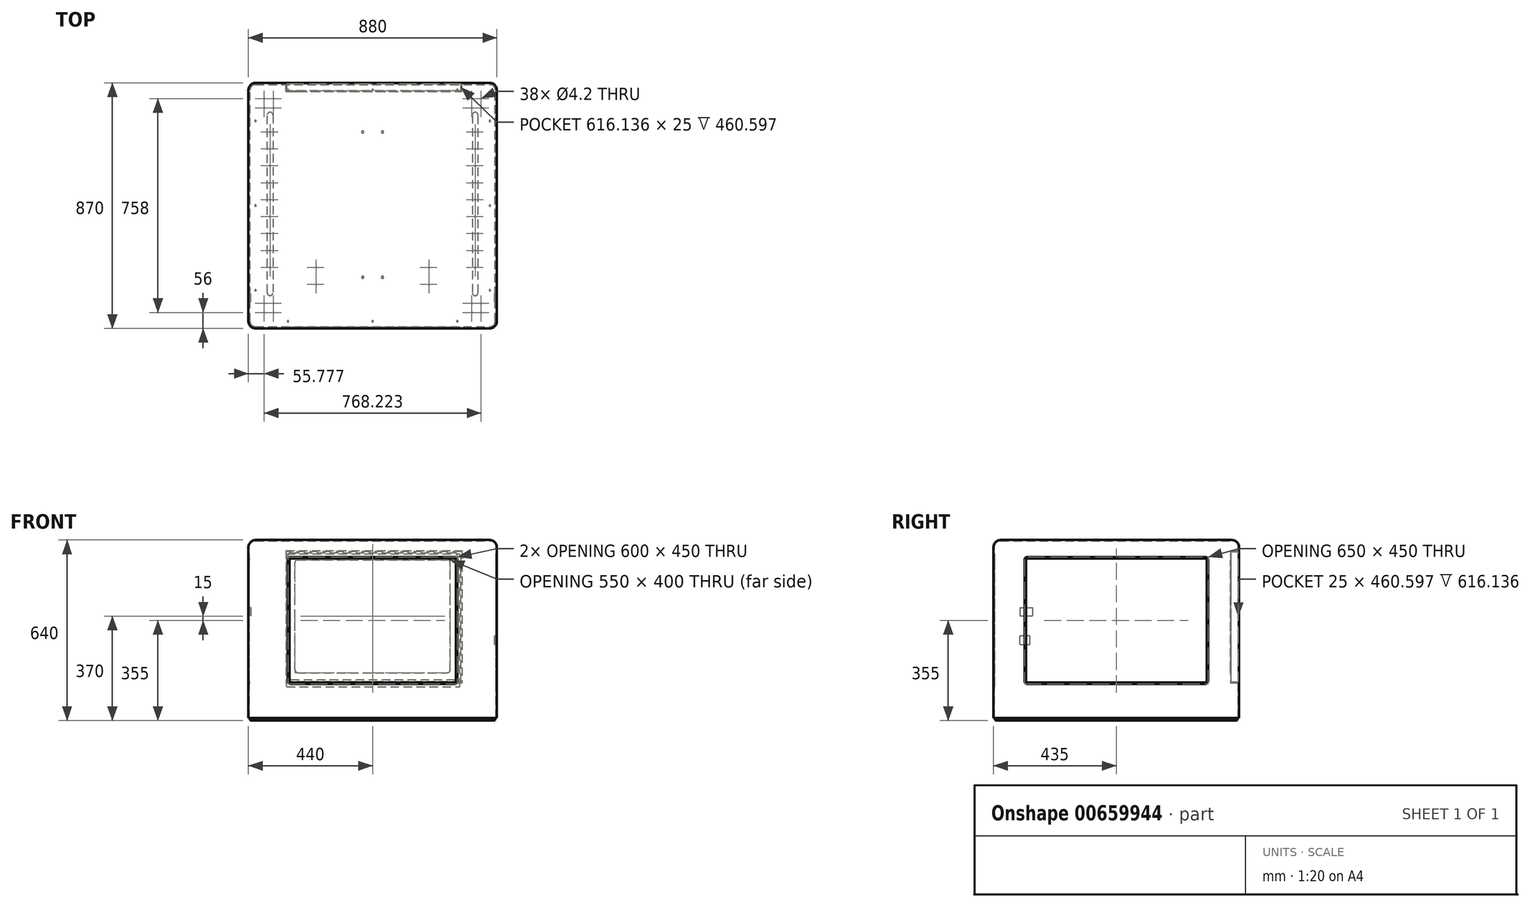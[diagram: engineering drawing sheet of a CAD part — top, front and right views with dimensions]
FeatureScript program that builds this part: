
annotation { "Feature Type Name" : "Feature", "Feature Type Description" : "" }
export const myFeature = defineFeature(function(context is Context, id is Id, definition is map)
    precondition{}
    {
        {
            var Q0;
            Q0=qCreatedBy(makeId("Top.planeOp"),FACE);
            var sketch = newSketch(context, id + "F0", { "sketchPlane" : qUnion([Q0])});
            skLineSegment(sketch, "E0.bottom", {"start": v(-440, -435) * mm, "end": v(440, -435) * mm});
            skLineSegment(sketch, "E0.top", {"start": v(-440, 435) * mm, "end": v(440, 435) * mm});
            skLineSegment(sketch, "E0.left", {"start": v(-440, -435) * mm, "end": v(-440, 435) * mm});
            skLineSegment(sketch, "E0.right", {"start": v(440, -435) * mm, "end": v(440, 435) * mm});
            skPoint(sketch, "E0.middle", {"position": v(0, 0) * mm});
            skSolve(sketch);
        }
        {
            var Q0;
            Q0 = qSketchRegion(id + "F0", true);
            extrude(context, id + "F1", {"entities" : qUnion([Q0]), "depth" : 630 * mm, "offsetDistance" : 25 * mm});
        }
        {
            var Q0;
            Q0=makeQuery(id+"F1.opExtrude","CAP_EDGE",EDGE,{"disambiguationData":[OSD([sQuery(id+"F0.wireOp",EDGE,"E0.right")])],"isStart":false});
            var Q1;
            Q1=makeQuery(id+"F1.opExtrude","CAP_EDGE",EDGE,{"disambiguationData":[OSD([sQuery(id+"F0.wireOp",EDGE,"E0.left")])],"isStart":false});
            fillet(context, id + "F2", {"entities" : qUnion([Q0, Q1]), "radius" : 25 * mm, "tangentPropagation" : true, "allowEdgeOverflow" : false});
        }
        {
            var Q0;
            Q0=makeQuery(id+"F1.opExtrude","CAP_EDGE",EDGE,{"disambiguationData":[OSD([sQuery(id+"F0.wireOp",EDGE,"E0.bottom")])],"isStart":false});
            var Q1;
            Q1=makeQuery(id+"F1.opExtrude","CAP_EDGE",EDGE,{"disambiguationData":[OSD([sQuery(id+"F0.wireOp",EDGE,"E0.top")])],"isStart":false});
            fillet(context, id + "F3", {"entities" : qUnion([Q0, Q1]), "radius" : 25 * mm, "tangentPropagation" : true, "allowEdgeOverflow" : false});
        }
        {
            var Q0;
            Q0=makeQuery(id+"F1.opExtrude","CAP_FACE",FACE,{"disambiguationData":[OSD([sQuery(id+"F0.wireOp",EDGE,"E0.bottom"),sQuery(id+"F0.wireOp",EDGE,"E0.top"),sQuery(id+"F0.wireOp",EDGE,"E0.left"),sQuery(id+"F0.wireOp",EDGE,"E0.right")])],"isStart":true});
            shell(context, id + "F4", {"entities" : qUnion([Q0]), "thickness" : 3 * mm});
        }
        {
            var Q0;
            Q0=makeQuery(id+"F1.opExtrude","SWEPT_FACE",FACE,{"disambiguationData":[OSD([sQuery(id+"F0.wireOp",EDGE,"E0.top")])]});
            var sketch = newSketch(context, id + "F5", { "sketchPlane" : qUnion([Q0])});
            skLineSegment(sketch, "E1.bottom", {"start": v(290, 135) * mm, "end": v(-290, 135) * mm});
            skLineSegment(sketch, "E1.top", {"start": v(290, 585) * mm, "end": v(-290, 585) * mm});
            skLineSegment(sketch, "E1.left", {"start": v(300, 145) * mm, "end": v(300, 575) * mm});
            skLineSegment(sketch, "E1.right", {"start": v(-300, 145) * mm, "end": v(-300, 575) * mm});
            skPoint(sketch, "E1.middle", {"position": v(0, 360) * mm});
            skPoint(sketch, "E2.visualSharp", {"position": v(-300, 585) * mm});
            skArc(sketch, "E2.filletArc", {"start": v(-290, 585) * mm, "mid": v(-297.07, 582.07) * mm, "end": v(-300, 575) * mm});
            skPoint(sketch, "E3.visualSharp", {"position": v(300, 585) * mm});
            skArc(sketch, "E3.filletArc", {"start": v(300, 575) * mm, "mid": v(297.07, 582.07) * mm, "end": v(290, 585) * mm});
            skPoint(sketch, "E4.visualSharp", {"position": v(300, 135) * mm});
            skArc(sketch, "E4.filletArc", {"start": v(290, 135) * mm, "mid": v(297.07, 137.93) * mm, "end": v(300, 145) * mm});
            skPoint(sketch, "E5.visualSharp", {"position": v(-300, 135) * mm});
            skArc(sketch, "E5.filletArc", {"start": v(-300, 145) * mm, "mid": v(-297.07, 137.93) * mm, "end": v(-290, 135) * mm});
            skSolve(sketch);
        }
        {
            var Q0;
            Q0 = qSketchRegion(id + "F5", true);
            extrude(context, id + "F6", {"entities" : qUnion([Q0]), "operationType" : NewBodyOperationType.REMOVE, "oppositeDirection" : true, "depth" : 25 * mm, "offsetDistance" : 25 * mm});
        }
        {
            var Q0;
            Q0=makeQuery(id+"F1.opExtrude","SWEPT_FACE",FACE,{"disambiguationData":[OSD([sQuery(id+"F0.wireOp",EDGE,"E0.bottom")])]});
            var sketch = newSketch(context, id + "F7", { "sketchPlane" : qUnion([Q0])});
            skLineSegment(sketch, "E6.bottom", {"start": v(290, 120) * mm, "end": v(-290, 120) * mm});
            skLineSegment(sketch, "E6.top", {"start": v(290, 570) * mm, "end": v(-290, 570) * mm});
            skLineSegment(sketch, "E6.left", {"start": v(300, 130) * mm, "end": v(300, 560) * mm});
            skLineSegment(sketch, "E6.right", {"start": v(-300, 130) * mm, "end": v(-300, 560) * mm});
            skPoint(sketch, "E6.middle", {"position": v(0, 345) * mm});
            skPoint(sketch, "E7.visualSharp", {"position": v(300, 570) * mm});
            skArc(sketch, "E7.filletArc", {"start": v(300, 560) * mm, "mid": v(297.07, 567.07) * mm, "end": v(290, 570) * mm});
            skPoint(sketch, "E8.visualSharp", {"position": v(-300, 570) * mm});
            skArc(sketch, "E8.filletArc", {"start": v(-290, 570) * mm, "mid": v(-297.07, 567.07) * mm, "end": v(-300, 560) * mm});
            skPoint(sketch, "E9.visualSharp", {"position": v(300, 120) * mm});
            skArc(sketch, "E9.filletArc", {"start": v(290, 120) * mm, "mid": v(297.07, 122.93) * mm, "end": v(300, 130) * mm});
            skPoint(sketch, "E10.visualSharp", {"position": v(-300, 120) * mm});
            skArc(sketch, "E10.filletArc", {"start": v(-300, 130) * mm, "mid": v(-297.07, 122.93) * mm, "end": v(-290, 120) * mm});
            skArc(sketch, "E11.0", {"start": v(295, 560) * mm, "mid": v(293.54, 563.54) * mm, "end": v(290, 565) * mm});
            skLineSegment(sketch, "E11.1", {"start": v(295, 130) * mm, "end": v(295, 560) * mm});
            skLineSegment(sketch, "E11.2", {"start": v(290, 565) * mm, "end": v(-290, 565) * mm});
            skArc(sketch, "E11.3", {"start": v(290, 125) * mm, "mid": v(293.54, 126.46) * mm, "end": v(295, 130) * mm});
            skArc(sketch, "E11.4", {"start": v(-290, 565) * mm, "mid": v(-293.54, 563.54) * mm, "end": v(-295, 560) * mm});
            skLineSegment(sketch, "E11.5", {"start": v(-295, 130) * mm, "end": v(-295, 560) * mm});
            skArc(sketch, "E11.6", {"start": v(-295, 130) * mm, "mid": v(-293.54, 126.46) * mm, "end": v(-290, 125) * mm});
            skLineSegment(sketch, "E11.7", {"start": v(290, 125) * mm, "end": v(-290, 125) * mm});
            skSolve(sketch);
        }
        {
            var Q0;
            Q0 = qSketchRegion(id + "F7", true);
            extrude(context, id + "F8", {"entities" : qUnion([Q0]), "operationType" : NewBodyOperationType.REMOVE, "oppositeDirection" : true, "depth" : 25 * mm, "offsetDistance" : 25 * mm});
        }
        {
            var Q0;
            {var subQ2=sQuery(id+"F0.wireOp",EDGE,"E0.bottom");var subQ3=makeQuery(id+"F1.opExtrude","SWEPT_FACE",FACE,{"disambiguationData":[OSD([subQ2])]});Q0=makeQuery(id+"F8.boolean.opBoolean","SPLIT",FACE,{"disambiguationData":[TD([makeQuery(id+"F8.opExtrude","SWEPT_FACE",FACE,{"disambiguationData":[OSD([sQuery(id+"F7.wireOp",EDGE,"E6.bottom")])]})])],"derivedFrom":makeQuery(id+"F4.opShell","OFFSET_FACE",FACE,{"disambiguationData":[OSD([subQ2]),TDD([subQ3])]})});}
            var sketch = newSketch(context, id + "F9", { "sketchPlane" : qUnion([Q0])});
            skLineSegment(sketch, "E12.bottom", {"start": v(304.63, 110.16) * mm, "end": v(-308.53, 110.16) * mm});
            skLineSegment(sketch, "E12.top", {"start": v(304.63, 580.55) * mm, "end": v(-308.53, 580.55) * mm});
            skLineSegment(sketch, "E12.left", {"start": v(304.63, 110.16) * mm, "end": v(304.63, 580.55) * mm});
            skLineSegment(sketch, "E12.right", {"start": v(-308.53, 110.16) * mm, "end": v(-308.53, 580.55) * mm});
            skSolve(sketch);
        }
        {
            var Q0;
            Q0 = qSketchRegion(id + "F9", true);
            extrude(context, id + "F10", {"entities" : qUnion([Q0]), "depth" : 2 * mm, "offsetDistance" : 25 * mm});
        }
        {
            var Q0;
            Q0=makeQuery(id+"F1.opExtrude","SWEPT_FACE",FACE,{"disambiguationData":[OSD([sQuery(id+"F0.wireOp",EDGE,"E0.right")])]});
            var sketch = newSketch(context, id + "F11", { "sketchPlane" : qUnion([Q0])});
            skLineSegment(sketch, "E13.bottom", {"start": v(315, 570) * mm, "end": v(-315, 570) * mm});
            skLineSegment(sketch, "E13.top", {"start": v(315, 120) * mm, "end": v(-315, 120) * mm});
            skLineSegment(sketch, "E13.left", {"start": v(325, 560) * mm, "end": v(325, 130) * mm});
            skLineSegment(sketch, "E13.right", {"start": v(-325, 560) * mm, "end": v(-325, 130) * mm});
            skPoint(sketch, "E13.middle", {"position": v(0, 345) * mm});
            skPoint(sketch, "E13.middle.positionSnap0", {"position": v(0, 0) * mm});
            skPoint(sketch, "E13.centerSnap0", {"position": v(0, 0) * mm});
            skPoint(sketch, "E14.visualSharp", {"position": v(325, 570) * mm});
            skArc(sketch, "E14.filletArc", {"start": v(325, 560) * mm, "mid": v(322.07, 567.07) * mm, "end": v(315, 570) * mm});
            skPoint(sketch, "E15.visualSharp", {"position": v(325, 120) * mm});
            skArc(sketch, "E15.filletArc", {"start": v(315, 120) * mm, "mid": v(322.07, 122.93) * mm, "end": v(325, 130) * mm});
            skPoint(sketch, "E16.visualSharp", {"position": v(-325, 120) * mm});
            skArc(sketch, "E16.filletArc", {"start": v(-325, 130) * mm, "mid": v(-322.07, 122.93) * mm, "end": v(-315, 120) * mm});
            skPoint(sketch, "E17.visualSharp", {"position": v(-325, 570) * mm});
            skArc(sketch, "E17.filletArc", {"start": v(-315, 570) * mm, "mid": v(-322.07, 567.07) * mm, "end": v(-325, 560) * mm});
            skArc(sketch, "E18.0", {"start": v(320, 560) * mm, "mid": v(318.54, 563.54) * mm, "end": v(315, 565) * mm});
            skLineSegment(sketch, "E18.1", {"start": v(320, 560) * mm, "end": v(320, 130) * mm});
            skLineSegment(sketch, "E18.2", {"start": v(315, 565) * mm, "end": v(-315, 565) * mm});
            skArc(sketch, "E18.3", {"start": v(315, 125) * mm, "mid": v(318.54, 126.46) * mm, "end": v(320, 130) * mm});
            skArc(sketch, "E18.4", {"start": v(-315, 565) * mm, "mid": v(-318.54, 563.54) * mm, "end": v(-320, 560) * mm});
            skLineSegment(sketch, "E18.5", {"start": v(-320, 560) * mm, "end": v(-320, 130) * mm});
            skArc(sketch, "E18.6", {"start": v(-320, 130) * mm, "mid": v(-318.54, 126.46) * mm, "end": v(-315, 125) * mm});
            skLineSegment(sketch, "E18.7", {"start": v(315, 125) * mm, "end": v(-315, 125) * mm});
            skSolve(sketch);
        }
        {
            var Q0;
            Q0 = qSketchRegion(id + "F11", true);
            extrude(context, id + "F12", {"entities" : qUnion([Q0]), "operationType" : NewBodyOperationType.REMOVE, "oppositeDirection" : true, "depth" : 2500 * mm, "offsetDistance" : 25 * mm});
        }
        {
            var Q0;
            {var subQ0=sQuery(id+"F0.wireOp",EDGE,"E0.left");Q0=makeQuery(id+"F12.boolean.opBoolean","SPLIT",FACE,{"disambiguationData":[TD([makeQuery(id+"F12.opExtrude","SWEPT_FACE",FACE,{"disambiguationData":[OSD([sQuery(id+"F11.wireOp",EDGE,"E13.bottom")])]})])],"derivedFrom":makeQuery(id+"F4.opShell","OFFSET_FACE",FACE,{"disambiguationData":[OSD([subQ0]),TDD([makeQuery(id+"F1.opExtrude","SWEPT_FACE",FACE,{"disambiguationData":[OSD([subQ0])]})])]})});}
            var sketch = newSketch(context, id + "F13", { "sketchPlane" : qUnion([Q0])});
            skLineSegment(sketch, "E19.bottom", {"start": v(-341.34, 390.67) * mm, "end": v(-296.45, 390.67) * mm});
            skLineSegment(sketch, "E19.top", {"start": v(-341.34, 361.64) * mm, "end": v(-296.45, 361.64) * mm});
            skLineSegment(sketch, "E19.left", {"start": v(-341.34, 390.67) * mm, "end": v(-341.34, 361.64) * mm});
            skLineSegment(sketch, "E19.right", {"start": v(-296.45, 390.67) * mm, "end": v(-296.45, 361.64) * mm});
            skSolve(sketch);
        }
        {
            var Q0;
            Q0 = qSketchRegion(id + "F13", true);
            extrude(context, id + "F14", {"entities" : qUnion([Q0]), "operationType" : NewBodyOperationType.ADD, "depth" : 5 * mm, "offsetDistance" : 25 * mm});
        }
        {
            var Q0;
            {var subQ1=sQuery(id+"F0.wireOp",EDGE,"E0.right");Q0=makeQuery(id+"F12.boolean.opBoolean","SPLIT",FACE,{"disambiguationData":[TD([makeQuery(id+"F12.opExtrude","SWEPT_FACE",FACE,{"disambiguationData":[OSD([sQuery(id+"F11.wireOp",EDGE,"E13.bottom")])]})])],"derivedFrom":makeQuery(id+"F4.opShell","OFFSET_FACE",FACE,{"disambiguationData":[OSD([subQ1]),TDD([makeQuery(id+"F1.opExtrude","SWEPT_FACE",FACE,{"disambiguationData":[OSD([subQ1])]})])]})});}
            var sketch = newSketch(context, id + "F15", { "sketchPlane" : qUnion([Q0])});
            skLineSegment(sketch, "E20.bottom", {"start": v(340.75, 259.87) * mm, "end": v(305.28, 259.87) * mm});
            skLineSegment(sketch, "E20.top", {"start": v(340.75, 291.6) * mm, "end": v(305.28, 291.6) * mm});
            skLineSegment(sketch, "E20.left", {"start": v(340.75, 259.87) * mm, "end": v(340.75, 291.6) * mm});
            skLineSegment(sketch, "E20.right", {"start": v(305.28, 259.87) * mm, "end": v(305.28, 291.6) * mm});
            skSolve(sketch);
        }
        {
            var Q0;
            Q0 = qSketchRegion(id + "F15", true);
            extrude(context, id + "F16", {"entities" : qUnion([Q0]), "operationType" : NewBodyOperationType.ADD, "depth" : 5 * mm, "offsetDistance" : 25 * mm});
        }
        {
            var Q0;
            Q0=makeQuery(id+"F1.opExtrude","CAP_FACE",FACE,{"disambiguationData":[OSD([sQuery(id+"F0.wireOp",EDGE,"E0.bottom"),sQuery(id+"F0.wireOp",EDGE,"E0.top"),sQuery(id+"F0.wireOp",EDGE,"E0.left"),sQuery(id+"F0.wireOp",EDGE,"E0.right")])],"isStart":true});
            var sketch = newSketch(context, id + "F17", { "sketchPlane" : qUnion([Q0])});
            skLineSegment(sketch, "E21.0", {"start": v(437, 410) * mm, "end": v(437, -410) * mm});
            skArc(sketch, "E22.0", {"start": v(415, -432) * mm, "mid": v(430.56, -425.56) * mm, "end": v(437, -410) * mm});
            skLineSegment(sketch, "E23.0", {"start": v(-415, -432) * mm, "end": v(415, -432) * mm});
            skArc(sketch, "E24.0", {"start": v(-437, -410) * mm, "mid": v(-430.56, -425.56) * mm, "end": v(-415, -432) * mm});
            skLineSegment(sketch, "E25.0", {"start": v(-437, 410) * mm, "end": v(-437, -410) * mm});
            skArc(sketch, "E26.0", {"start": v(-415, 432) * mm, "mid": v(-430.56, 425.56) * mm, "end": v(-437, 410) * mm});
            skLineSegment(sketch, "E27.0", {"start": v(-415, 432) * mm, "end": v(415, 432) * mm});
            skArc(sketch, "E28.0", {"start": v(437, 410) * mm, "mid": v(430.56, 425.56) * mm, "end": v(415, 432) * mm});
            skArc(sketch, "E29.0", {"start": v(434, 410) * mm, "mid": v(428.44, 423.44) * mm, "end": v(415, 429) * mm});
            skLineSegment(sketch, "E29.1", {"start": v(-415, 429) * mm, "end": v(415, 429) * mm});
            skLineSegment(sketch, "E29.2", {"start": v(434, 410) * mm, "end": v(434, -410) * mm});
            skArc(sketch, "E29.3", {"start": v(-415, 429) * mm, "mid": v(-428.44, 423.44) * mm, "end": v(-434, 410) * mm});
            skArc(sketch, "E29.4", {"start": v(415, -429) * mm, "mid": v(428.44, -423.44) * mm, "end": v(434, -410) * mm});
            skLineSegment(sketch, "E29.5", {"start": v(-415, -429) * mm, "end": v(415, -429) * mm});
            skArc(sketch, "E29.6", {"start": v(-434, -410) * mm, "mid": v(-428.44, -423.44) * mm, "end": v(-415, -429) * mm});
            skLineSegment(sketch, "E29.7", {"start": v(-434, 410) * mm, "end": v(-434, -410) * mm});
            skLineSegment(sketch, "E30.bottom", {"start": v(-384, 379) * mm, "end": v(-351, 379) * mm, "construction": true});
            skLineSegment(sketch, "E30.top", {"start": v(-384, 346) * mm, "end": v(-351, 346) * mm, "construction": true});
            skLineSegment(sketch, "E30.left", {"start": v(-384, 379) * mm, "end": v(-384, 346) * mm, "construction": true});
            skLineSegment(sketch, "E30.right", {"start": v(-351, 379) * mm, "end": v(-351, 346) * mm, "construction": true});
            skCircle(sketch, "E31", {"center": v(-384, 379) * mm, "radius": 2.5 * mm});
            skCircle(sketch, "E32", {"center": v(-351, 379) * mm, "radius": 2.5 * mm});
            skCircle(sketch, "E33", {"center": v(-351, 346) * mm, "radius": 2.5 * mm});
            skCircle(sketch, "E34", {"center": v(-384, 346) * mm, "radius": 2.5 * mm});
            skCircle(sketch, "E35", {"center": v(351, 379) * mm, "radius": 2.5 * mm});
            skCircle(sketch, "E36", {"center": v(384, 379) * mm, "radius": 2.5 * mm});
            skCircle(sketch, "E37", {"center": v(384, 346) * mm, "radius": 2.5 * mm});
            skCircle(sketch, "E38", {"center": v(351, 346) * mm, "radius": 2.5 * mm});
            skCircle(sketch, "E39", {"center": v(-384, -346) * mm, "radius": 2.5 * mm});
            skCircle(sketch, "E40", {"center": v(-351, -379) * mm, "radius": 2.5 * mm});
            skCircle(sketch, "E41", {"center": v(-351, -346) * mm, "radius": 2.5 * mm});
            skCircle(sketch, "E42", {"center": v(-384.22, -379) * mm, "radius": 2.5 * mm});
            skCircle(sketch, "E43", {"center": v(351, -346) * mm, "radius": 2.5 * mm});
            skCircle(sketch, "E44", {"center": v(384, -346) * mm, "radius": 2.5 * mm});
            skCircle(sketch, "E45", {"center": v(384, -379) * mm, "radius": 2.5 * mm});
            skCircle(sketch, "E46", {"center": v(351, -379) * mm, "radius": 2.5 * mm});
            skSolve(sketch);
        }
        {
            var Q0;
            Q0=makeQuery(id+"F17.imprint","IMPRINT",FACE,{"disambiguationData":[TD([[makeQuery(id+"F17.imprint","IMPRINT",EDGE,{"derivedFrom":sQuery(id+"F17.wireOp",EDGE,"E29.0")}),1.0]])]});
            var Q1;
            Q1=makeQuery(id+"F17.imprint","IMPRINT",FACE,{"disambiguationData":[TD([[makeQuery(id+"F17.imprint","IMPRINT",EDGE,{"derivedFrom":sQuery(id+"F17.wireOp",EDGE,"E31")}),1.0]])]});
            var Q2;
            Q2=makeQuery(id+"F17.imprint","IMPRINT",FACE,{"disambiguationData":[TD([[makeQuery(id+"F17.imprint","IMPRINT",EDGE,{"derivedFrom":sQuery(id+"F17.wireOp",EDGE,"E32")}),1.0]])]});
            var Q3;
            Q3=makeQuery(id+"F17.imprint","IMPRINT",FACE,{"disambiguationData":[TD([[makeQuery(id+"F17.imprint","IMPRINT",EDGE,{"derivedFrom":sQuery(id+"F17.wireOp",EDGE,"E33")}),1.0]])]});
            var Q4;
            Q4=makeQuery(id+"F17.imprint","IMPRINT",FACE,{"disambiguationData":[TD([[makeQuery(id+"F17.imprint","IMPRINT",EDGE,{"derivedFrom":sQuery(id+"F17.wireOp",EDGE,"E34")}),1.0]])]});
            var Q5;
            Q5=makeQuery(id+"F17.imprint","IMPRINT",FACE,{"disambiguationData":[TD([[makeQuery(id+"F17.imprint","IMPRINT",EDGE,{"derivedFrom":sQuery(id+"F17.wireOp",EDGE,"E39")}),1.0]])]});
            var Q6;
            Q6=makeQuery(id+"F17.imprint","IMPRINT",FACE,{"disambiguationData":[TD([[makeQuery(id+"F17.imprint","IMPRINT",EDGE,{"derivedFrom":sQuery(id+"F17.wireOp",EDGE,"E41")}),1.0]])]});
            var Q7;
            Q7=makeQuery(id+"F17.imprint","IMPRINT",FACE,{"disambiguationData":[TD([[makeQuery(id+"F17.imprint","IMPRINT",EDGE,{"derivedFrom":sQuery(id+"F17.wireOp",EDGE,"E40")}),1.0]])]});
            var Q8;
            Q8=makeQuery(id+"F17.imprint","IMPRINT",FACE,{"disambiguationData":[TD([[makeQuery(id+"F17.imprint","IMPRINT",EDGE,{"derivedFrom":sQuery(id+"F17.wireOp",EDGE,"E42")}),1.0]])]});
            var Q9;
            Q9=makeQuery(id+"F17.imprint","IMPRINT",FACE,{"disambiguationData":[TD([[makeQuery(id+"F17.imprint","IMPRINT",EDGE,{"derivedFrom":sQuery(id+"F17.wireOp",EDGE,"E45")}),1.0]])]});
            var Q10;
            Q10=makeQuery(id+"F17.imprint","IMPRINT",FACE,{"disambiguationData":[TD([[makeQuery(id+"F17.imprint","IMPRINT",EDGE,{"derivedFrom":sQuery(id+"F17.wireOp",EDGE,"E44")}),1.0]])]});
            var Q11;
            Q11=makeQuery(id+"F17.imprint","IMPRINT",FACE,{"disambiguationData":[TD([[makeQuery(id+"F17.imprint","IMPRINT",EDGE,{"derivedFrom":sQuery(id+"F17.wireOp",EDGE,"E43")}),1.0]])]});
            var Q12;
            Q12=makeQuery(id+"F17.imprint","IMPRINT",FACE,{"disambiguationData":[TD([[makeQuery(id+"F17.imprint","IMPRINT",EDGE,{"derivedFrom":sQuery(id+"F17.wireOp",EDGE,"E46")}),1.0]])]});
            var Q13;
            Q13=makeQuery(id+"F17.imprint","IMPRINT",FACE,{"disambiguationData":[TD([[makeQuery(id+"F17.imprint","IMPRINT",EDGE,{"derivedFrom":sQuery(id+"F17.wireOp",EDGE,"E35")}),1.0]])]});
            var Q14;
            Q14=makeQuery(id+"F17.imprint","IMPRINT",FACE,{"disambiguationData":[TD([[makeQuery(id+"F17.imprint","IMPRINT",EDGE,{"derivedFrom":sQuery(id+"F17.wireOp",EDGE,"E36")}),1.0]])]});
            var Q15;
            Q15=makeQuery(id+"F17.imprint","IMPRINT",FACE,{"disambiguationData":[TD([[makeQuery(id+"F17.imprint","IMPRINT",EDGE,{"derivedFrom":sQuery(id+"F17.wireOp",EDGE,"E37")}),1.0]])]});
            var Q16;
            Q16=makeQuery(id+"F17.imprint","IMPRINT",FACE,{"disambiguationData":[TD([[makeQuery(id+"F17.imprint","IMPRINT",EDGE,{"derivedFrom":sQuery(id+"F17.wireOp",EDGE,"E38")}),1.0]])]});
            extrude(context, id + "F18", {"entities" : qUnion([Q0, Q1, Q2, Q3, Q4, Q5, Q6, Q7, Q8, Q9, Q10, Q11, Q12, Q13, Q14, Q15, Q16]), "depth" : 10 * mm, "offsetDistance" : 25 * mm});
        }
        {
            var Q0;
            Q0 = qSketchRegion(id + "F17", true);
            extrude(context, id + "F19", {"entities" : qUnion([Q0]), "operationType" : NewBodyOperationType.REMOVE, "oppositeDirection" : true, "depth" : 5 * mm, "offsetDistance" : 25 * mm});
        }
        {
            var Q0;
            Q0=makeQuery(id+"F18.opExtrude","CAP_FACE",FACE,{"disambiguationData":[OSD([sQuery(id+"F17.wireOp",EDGE,"E29.0"),sQuery(id+"F17.wireOp",EDGE,"E29.1"),sQuery(id+"F17.wireOp",EDGE,"E29.2"),sQuery(id+"F17.wireOp",EDGE,"E29.3"),sQuery(id+"F17.wireOp",EDGE,"E29.4"),sQuery(id+"F17.wireOp",EDGE,"E29.5"),sQuery(id+"F17.wireOp",EDGE,"E29.6"),sQuery(id+"F17.wireOp",EDGE,"E29.7"),sQuery(id+"F17.wireOp",EDGE,"E31"),sQuery(id+"F17.wireOp",EDGE,"E32"),sQuery(id+"F17.wireOp",EDGE,"E33"),sQuery(id+"F17.wireOp",EDGE,"E34"),sQuery(id+"F17.wireOp",EDGE,"E35"),sQuery(id+"F17.wireOp",EDGE,"E36"),sQuery(id+"F17.wireOp",EDGE,"E37"),sQuery(id+"F17.wireOp",EDGE,"E38"),sQuery(id+"F17.wireOp",EDGE,"E39"),sQuery(id+"F17.wireOp",EDGE,"E40"),sQuery(id+"F17.wireOp",EDGE,"E41"),sQuery(id+"F17.wireOp",EDGE,"E42"),sQuery(id+"F17.wireOp",EDGE,"E43"),sQuery(id+"F17.wireOp",EDGE,"E44"),sQuery(id+"F17.wireOp",EDGE,"E45"),sQuery(id+"F17.wireOp",EDGE,"E46")])],"isStart":false});
            var sketch = newSketch(context, id + "F20", { "sketchPlane" : qUnion([Q0])});
            skCircle(sketch, "E47", {"center": v(-35, 254) * mm, "radius": 4 * mm});
            skCircle(sketch, "E48", {"center": v(35, 254) * mm, "radius": 4 * mm});
            skCircle(sketch, "E49", {"center": v(35, -261) * mm, "radius": 4 * mm});
            skCircle(sketch, "E50", {"center": v(-35, -261) * mm, "radius": 4 * mm});
            skSolve(sketch);
        }
        {
            var Q0;
            Q0 = qSketchRegion(id + "F20", true);
            extrude(context, id + "F21", {"entities" : qUnion([Q0]), "operationType" : NewBodyOperationType.REMOVE, "oppositeDirection" : true, "depth" : 5 * mm, "offsetDistance" : 25 * mm});
        }
        {
            var Q0;
            Q0=makeQuery(id+"F21.boolean.opBoolean","COPY",FACE,{"derivedFrom":makeQuery(id+"F21.opExtrude","CAP_FACE",FACE,{"disambiguationData":[OSD([sQuery(id+"F20.wireOp",EDGE,"E47")])],"isStart":false})});
            var sketch = newSketch(context, id + "F22", { "sketchPlane" : qUnion([Q0])});
            skCircle(sketch, "E51.0.0", {"center": v(-35, 254) * mm, "radius": 4 * mm});
            skCircle(sketch, "E52.0.0", {"center": v(35, 254) * mm, "radius": 4 * mm});
            skCircle(sketch, "E53.0.0", {"center": v(-35, -261) * mm, "radius": 4 * mm});
            skCircle(sketch, "E54.0.0", {"center": v(35, -261) * mm, "radius": 4 * mm});
            skSolve(sketch);
        }
        {
            var Q0;
            Q0=makeQuery(id+"F18.opExtrude","CAP_FACE",FACE,{"disambiguationData":[OSD([sQuery(id+"F17.wireOp",EDGE,"E29.0"),sQuery(id+"F17.wireOp",EDGE,"E29.1"),sQuery(id+"F17.wireOp",EDGE,"E29.2"),sQuery(id+"F17.wireOp",EDGE,"E29.3"),sQuery(id+"F17.wireOp",EDGE,"E29.4"),sQuery(id+"F17.wireOp",EDGE,"E29.5"),sQuery(id+"F17.wireOp",EDGE,"E29.6"),sQuery(id+"F17.wireOp",EDGE,"E29.7"),sQuery(id+"F17.wireOp",EDGE,"E31"),sQuery(id+"F17.wireOp",EDGE,"E32"),sQuery(id+"F17.wireOp",EDGE,"E33"),sQuery(id+"F17.wireOp",EDGE,"E34"),sQuery(id+"F17.wireOp",EDGE,"E35"),sQuery(id+"F17.wireOp",EDGE,"E36"),sQuery(id+"F17.wireOp",EDGE,"E37"),sQuery(id+"F17.wireOp",EDGE,"E38"),sQuery(id+"F17.wireOp",EDGE,"E39"),sQuery(id+"F17.wireOp",EDGE,"E40"),sQuery(id+"F17.wireOp",EDGE,"E41"),sQuery(id+"F17.wireOp",EDGE,"E42"),sQuery(id+"F17.wireOp",EDGE,"E43"),sQuery(id+"F17.wireOp",EDGE,"E44"),sQuery(id+"F17.wireOp",EDGE,"E45"),sQuery(id+"F17.wireOp",EDGE,"E46")])],"isStart":true});
            var sketch = newSketch(context, id + "F23", { "sketchPlane" : qUnion([Q0])});
            skLineSegment(sketch, "E55", {"start": v(373.38, -309) * mm, "end": v(373.38, 321) * mm});
            skLineSegment(sketch, "E56", {"start": v(353.38, 321) * mm, "end": v(353.38, -309) * mm});
            skLineSegment(sketch, "E57.MirrorCS", {"start": v(-353.38, 321) * mm, "end": v(-353.38, -309) * mm});
            skLineSegment(sketch, "E58.MirrorCS", {"start": v(-373.38, -309) * mm, "end": v(-373.38, 321) * mm});
            skArc(sketch, "E59", {"start": v(373.38, 321) * mm, "mid": v(363.38, 331) * mm, "end": v(353.38, 321) * mm});
            skArc(sketch, "E60", {"start": v(353.38, -309) * mm, "mid": v(363.38, -319) * mm, "end": v(373.38, -309) * mm});
            skArc(sketch, "E61", {"start": v(-353.38, 321) * mm, "mid": v(-363.38, 331) * mm, "end": v(-373.38, 321) * mm});
            skArc(sketch, "E62", {"start": v(-373.38, -309) * mm, "mid": v(-363.38, -319) * mm, "end": v(-353.38, -309) * mm});
            skPoint(sketch, "E63.orphan", {"position": v(-373.38, -309) * mm});
            skPoint(sketch, "E64.MirrorCS.start.orphan", {"position": v(-353.38, -309) * mm});
            skPoint(sketch, "E65.orphan", {"position": v(-353.38, 321) * mm});
            skSolve(sketch);
        }
        {
            var Q0;
            Q0 = qSketchRegion(id + "F23", true);
            extrude(context, id + "F24", {"entities" : qUnion([Q0]), "operationType" : NewBodyOperationType.REMOVE, "oppositeDirection" : true, "depth" : 2 * mm, "offsetDistance" : 25 * mm});
        }
        {
            var Q0;
            Q0=makeQuery(id+"F24.boolean.opBoolean","COPY",FACE,{"derivedFrom":makeQuery(id+"F24.opExtrude","CAP_FACE",FACE,{"disambiguationData":[OSD([sQuery(id+"F23.wireOp",EDGE,"E55"),sQuery(id+"F23.wireOp",EDGE,"MjliI0Ah-OMxi-VJqQ-nH6Z-UFhm3DybuUQN"),sQuery(id+"F23.wireOp",EDGE,"E56"),sQuery(id+"F23.wireOp",EDGE,"Od6bIoql-sXcw-kLId-crT9-5d1gGYvD4wC0")])],"isStart":false})});
            var sketch = newSketch(context, id + "F25", { "sketchPlane" : qUnion([Q0])});
            skCircle(sketch, "E66", {"center": v(363.38, -219) * mm, "radius": 2.75 * mm});
            skPoint(sketch, "E66.centerSnap0", {"position": v(363.38, -279) * mm});
            skCircle(sketch, "E67", {"center": v(363.38, -159) * mm, "radius": 2.75 * mm});
            skCircle(sketch, "E68", {"center": v(363.38, -99) * mm, "radius": 2.75 * mm});
            skCircle(sketch, "E69", {"center": v(363.38, -39) * mm, "radius": 2.75 * mm});
            skCircle(sketch, "E70", {"center": v(363.38, 21) * mm, "radius": 2.75 * mm});
            skCircle(sketch, "E71", {"center": v(363.38, 81) * mm, "radius": 2.75 * mm});
            skCircle(sketch, "E72", {"center": v(363.38, 141) * mm, "radius": 2.75 * mm});
            skCircle(sketch, "E73", {"center": v(363.38, 201) * mm, "radius": 2.75 * mm});
            skCircle(sketch, "E74", {"center": v(363.38, 261) * mm, "radius": 2.75 * mm});
            skCircle(sketch, "E75.MirrorC", {"center": v(-363.38, -219) * mm, "radius": 2.75 * mm});
            skCircle(sketch, "E76.MirrorC", {"center": v(-363.38, -159) * mm, "radius": 2.75 * mm});
            skCircle(sketch, "E77.MirrorC", {"center": v(-363.38, -99) * mm, "radius": 2.75 * mm});
            skCircle(sketch, "E78.MirrorC", {"center": v(-363.38, -39) * mm, "radius": 2.75 * mm});
            skCircle(sketch, "E79.MirrorC", {"center": v(-363.38, 21) * mm, "radius": 2.75 * mm});
            skCircle(sketch, "E80.MirrorC", {"center": v(-363.38, 81) * mm, "radius": 2.75 * mm});
            skCircle(sketch, "E81.MirrorC", {"center": v(-363.38, 261) * mm, "radius": 2.75 * mm});
            skCircle(sketch, "E82.MirrorC", {"center": v(-363.38, 201) * mm, "radius": 2.75 * mm});
            skCircle(sketch, "E83.MirrorC", {"center": v(-363.38, 141) * mm, "radius": 2.75 * mm});
            skSolve(sketch);
        }
        {
            var Q0;
            Q0=makeQuery(id+"F18.opExtrude","SWEPT_FACE",FACE,{"disambiguationData":[OSD([sQuery(id+"F17.wireOp",EDGE,"E29.5")])]});
            var sketch = newSketch(context, id + "F26", { "sketchPlane" : qUnion([Q0])});
            skLineSegment(sketch, "E84", {"start": v(0, -5.47) * mm, "end": v(3.29, 0) * mm});
            skPoint(sketch, "E84.startSnap0", {"position": v(0, 0) * mm});
            skLineSegment(sketch, "E85", {"start": v(3.29, 0) * mm, "end": v(-3.32, 0) * mm});
            skLineSegment(sketch, "E86", {"start": v(-3.32, 0) * mm, "end": v(0, -2.33) * mm});
            skLineSegment(sketch, "E87", {"start": v(0, -2.33) * mm, "end": v(0, -5.47) * mm});
            skSolve(sketch);
        }
        {
            var Q0;
            Q0=makeQuery(id+"F18.opExtrude","CAP_FACE",FACE,{"disambiguationData":[OSD([sQuery(id+"F17.wireOp",EDGE,"E29.0"),sQuery(id+"F17.wireOp",EDGE,"E29.1"),sQuery(id+"F17.wireOp",EDGE,"E29.2"),sQuery(id+"F17.wireOp",EDGE,"E29.3"),sQuery(id+"F17.wireOp",EDGE,"E29.4"),sQuery(id+"F17.wireOp",EDGE,"E29.5"),sQuery(id+"F17.wireOp",EDGE,"E29.6"),sQuery(id+"F17.wireOp",EDGE,"E29.7"),sQuery(id+"F17.wireOp",EDGE,"E31"),sQuery(id+"F17.wireOp",EDGE,"E32"),sQuery(id+"F17.wireOp",EDGE,"E33"),sQuery(id+"F17.wireOp",EDGE,"E34"),sQuery(id+"F17.wireOp",EDGE,"E35"),sQuery(id+"F17.wireOp",EDGE,"E36"),sQuery(id+"F17.wireOp",EDGE,"E37"),sQuery(id+"F17.wireOp",EDGE,"E38"),sQuery(id+"F17.wireOp",EDGE,"E39"),sQuery(id+"F17.wireOp",EDGE,"E40"),sQuery(id+"F17.wireOp",EDGE,"E41"),sQuery(id+"F17.wireOp",EDGE,"E42"),sQuery(id+"F17.wireOp",EDGE,"E43"),sQuery(id+"F17.wireOp",EDGE,"E44"),sQuery(id+"F17.wireOp",EDGE,"E45"),sQuery(id+"F17.wireOp",EDGE,"E46")])],"isStart":false});
            var sketch = newSketch(context, id + "F27", { "sketchPlane" : qUnion([Q0])});
            skCircle(sketch, "E88", {"center": v(200, 219) * mm, "radius": 2.88 * mm});
            skCircle(sketch, "E89", {"center": v(-200, 219) * mm, "radius": 2.75 * mm});
            skCircle(sketch, "E90", {"center": v(-200, 279) * mm, "radius": 2.5 * mm});
            skCircle(sketch, "E91", {"center": v(200, 279) * mm, "radius": 2.45 * mm});
            skSolve(sketch);
        }
        {
            var Q0;
            Q0=makeQuery(id+"F18.opExtrude","CAP_FACE",FACE,{"disambiguationData":[OSD([sQuery(id+"F17.wireOp",EDGE,"E29.0"),sQuery(id+"F17.wireOp",EDGE,"E29.1"),sQuery(id+"F17.wireOp",EDGE,"E29.2"),sQuery(id+"F17.wireOp",EDGE,"E29.3"),sQuery(id+"F17.wireOp",EDGE,"E29.4"),sQuery(id+"F17.wireOp",EDGE,"E29.5"),sQuery(id+"F17.wireOp",EDGE,"E29.6"),sQuery(id+"F17.wireOp",EDGE,"E29.7"),sQuery(id+"F17.wireOp",EDGE,"E31"),sQuery(id+"F17.wireOp",EDGE,"E32"),sQuery(id+"F17.wireOp",EDGE,"E33"),sQuery(id+"F17.wireOp",EDGE,"E34"),sQuery(id+"F17.wireOp",EDGE,"E35"),sQuery(id+"F17.wireOp",EDGE,"E36"),sQuery(id+"F17.wireOp",EDGE,"E37"),sQuery(id+"F17.wireOp",EDGE,"E38"),sQuery(id+"F17.wireOp",EDGE,"E39"),sQuery(id+"F17.wireOp",EDGE,"E40"),sQuery(id+"F17.wireOp",EDGE,"E41"),sQuery(id+"F17.wireOp",EDGE,"E42"),sQuery(id+"F17.wireOp",EDGE,"E43"),sQuery(id+"F17.wireOp",EDGE,"E44"),sQuery(id+"F17.wireOp",EDGE,"E45"),sQuery(id+"F17.wireOp",EDGE,"E46")])],"isStart":false});
            var sketch = newSketch(context, id + "F28", { "sketchPlane" : qUnion([Q0])});
            skCircle(sketch, "E92", {"center": v(415, 0) * mm, "radius": 2.5 * mm});
            skPoint(sketch, "E92.centerSnap0", {"position": v(434, 0) * mm});
            skCircle(sketch, "E93", {"center": v(415, -300) * mm, "radius": 2.5 * mm});
            skCircle(sketch, "E94", {"center": v(415, 300) * mm, "radius": 2.5 * mm});
            skCircle(sketch, "E95", {"center": v(-415, 0) * mm, "radius": 2.5 * mm});
            skPoint(sketch, "E95.centerSnap0", {"position": v(-434, 0) * mm});
            skCircle(sketch, "E96", {"center": v(-415, -300) * mm, "radius": 2.5 * mm});
            skCircle(sketch, "E97", {"center": v(-415, 300) * mm, "radius": 2.5 * mm});
            skCircle(sketch, "E98", {"center": v(0, 410) * mm, "radius": 2.5 * mm});
            skPoint(sketch, "E98.centerSnap0", {"position": v(0, 429) * mm});
            skCircle(sketch, "E99", {"center": v(-300, 410) * mm, "radius": 2.5 * mm});
            skCircle(sketch, "E100", {"center": v(300, 410) * mm, "radius": 2.5 * mm});
            skCircle(sketch, "E101", {"center": v(0, -410) * mm, "radius": 2.5 * mm});
            skPoint(sketch, "E101.centerSnap0", {"position": v(0, -429) * mm});
            skCircle(sketch, "E102", {"center": v(-300, -410) * mm, "radius": 2.5 * mm});
            skCircle(sketch, "E103", {"center": v(300, -410) * mm, "radius": 2.5 * mm});
            skSolve(sketch);
        }
        {
            var Q0;
            Q0 = qSketchRegion(id + "F28", true);
            extrude(context, id + "F29", {"entities" : qUnion([Q0]), "operationType" : NewBodyOperationType.REMOVE, "oppositeDirection" : true, "depth" : 25 * mm, "offsetDistance" : 25 * mm});
        }
        {
            var Q0;
            Q0=sQuery(id+"F17.wireOp",VERTEX,"E35.center");
            var Q1;
            Q1=sQuery(id+"F17.wireOp",VERTEX,"E38.center");
            var Q2;
            Q2=sQuery(id+"F17.wireOp",VERTEX,"E36.center");
            var Q3;
            Q3=sQuery(id+"F17.wireOp",VERTEX,"E37.center");
            var Q4;
            Q4=sQuery(id+"F17.wireOp",VERTEX,"E30.left.start");
            var Q5;
            Q5=sQuery(id+"F17.wireOp",VERTEX,"E30.bottom.end");
            var Q6;
            Q6=sQuery(id+"F17.wireOp",VERTEX,"E30.top.end");
            var Q7;
            Q7=sQuery(id+"F17.wireOp",VERTEX,"E34.center");
            var Q8;
            Q8=sQuery(id+"F17.wireOp",VERTEX,"E42.center");
            var Q9;
            Q9=sQuery(id+"F17.wireOp",VERTEX,"E40.center");
            var Q10;
            Q10=sQuery(id+"F17.wireOp",VERTEX,"E41.center");
            var Q11;
            Q11=sQuery(id+"F17.wireOp",VERTEX,"E39.center");
            var Q12;
            Q12=sQuery(id+"F17.wireOp",VERTEX,"E44.center");
            var Q13;
            Q13=sQuery(id+"F17.wireOp",VERTEX,"E45.center");
            var Q14;
            Q14=sQuery(id+"F17.wireOp",VERTEX,"E46.center");
            var Q15;
            Q15=sQuery(id+"F17.wireOp",VERTEX,"E43.center");
            var Q16;
            Q16=makeQuery(id+"F18.opExtrude","SWEPT_BODY",BODY,{"disambiguationData":[OSD([sQuery(id+"F17.wireOp",EDGE,"E29.0"),sQuery(id+"F17.wireOp",EDGE,"E29.1"),sQuery(id+"F17.wireOp",EDGE,"E29.2"),sQuery(id+"F17.wireOp",EDGE,"E29.3"),sQuery(id+"F17.wireOp",EDGE,"E29.4"),sQuery(id+"F17.wireOp",EDGE,"E29.5"),sQuery(id+"F17.wireOp",EDGE,"E29.6"),sQuery(id+"F17.wireOp",EDGE,"E29.7")])]});
            hole(context, id + "F30", {"style" : HoleStyle.SIMPLE, "endStyle" : HoleEndStyle.THROUGH, "oppositeDirection" : true, "standardTappedOrClearance" : lookupTablePath({ "standard" : "ISO", "engagement" : "75%", "pitch" : "0.8 mm", "size" : "M5", "type" : "Tapped" }), "standardBlindInLast" : lookupTablePath({ "standard" : "ISO", "engagement" : "75%", "pitch" : "0.8 mm", "size" : "M5", "type" : "Tapped" }), "holeDiameter" : 4.2 * mm, "majorDiameter" : 5 * mm, "showTappedDepth" : true, "isTappedThrough" : true, "tappedDepth" : 10.4 * mm, "tapClearance" : 3, "locations" : qUnion([Q0, Q1, Q2, Q3, Q4, Q5, Q6, Q7, Q8, Q9, Q10, Q11, Q12, Q13, Q14, Q15]), "scope" : qUnion([Q16])});
        }
        {
            var Q0;
            Q0=sQuery(id+"F25.wireOp",VERTEX,"E66.center");
            var Q1;
            Q1=sQuery(id+"F25.wireOp",VERTEX,"E67.center");
            var Q2;
            Q2=sQuery(id+"F25.wireOp",VERTEX,"E68.center");
            var Q3;
            Q3=sQuery(id+"F25.wireOp",VERTEX,"E69.center");
            var Q4;
            Q4=sQuery(id+"F25.wireOp",VERTEX,"E70.center");
            var Q5;
            Q5=sQuery(id+"F25.wireOp",VERTEX,"E71.center");
            var Q6;
            Q6=sQuery(id+"F25.wireOp",VERTEX,"E72.center");
            var Q7;
            Q7=sQuery(id+"F25.wireOp",VERTEX,"E73.center");
            var Q8;
            Q8=sQuery(id+"F25.wireOp",VERTEX,"E74.center");
            var Q9;
            Q9=sQuery(id+"F25.wireOp",VERTEX,"E75.MirrorC.center");
            var Q10;
            Q10=sQuery(id+"F25.wireOp",VERTEX,"E76.MirrorC.center");
            var Q11;
            Q11=sQuery(id+"F25.wireOp",VERTEX,"E77.MirrorC.center");
            var Q12;
            Q12=sQuery(id+"F25.wireOp",VERTEX,"E78.MirrorC.center");
            var Q13;
            Q13=sQuery(id+"F25.wireOp",VERTEX,"E79.MirrorC.center");
            var Q14;
            Q14=sQuery(id+"F25.wireOp",VERTEX,"E80.MirrorC.center");
            var Q15;
            Q15=sQuery(id+"F25.wireOp",VERTEX,"E83.MirrorC.center");
            var Q16;
            Q16=sQuery(id+"F25.wireOp",VERTEX,"E82.MirrorC.center");
            var Q17;
            Q17=sQuery(id+"F25.wireOp",VERTEX,"E81.MirrorC.center");
            var Q18;
            Q18=makeQuery(id+"F18.opExtrude","SWEPT_BODY",BODY,{"disambiguationData":[OSD([sQuery(id+"F17.wireOp",EDGE,"E29.0"),sQuery(id+"F17.wireOp",EDGE,"E29.1"),sQuery(id+"F17.wireOp",EDGE,"E29.2"),sQuery(id+"F17.wireOp",EDGE,"E29.3"),sQuery(id+"F17.wireOp",EDGE,"E29.4"),sQuery(id+"F17.wireOp",EDGE,"E29.5"),sQuery(id+"F17.wireOp",EDGE,"E29.6"),sQuery(id+"F17.wireOp",EDGE,"E29.7")])]});
            hole(context, id + "F31", {"style" : HoleStyle.SIMPLE, "endStyle" : HoleEndStyle.THROUGH, "standardTappedOrClearance" : lookupTablePath({ "standard" : "ISO", "engagement" : "75%", "pitch" : "0.8 mm", "size" : "M5", "type" : "Tapped" }), "standardBlindInLast" : lookupTablePath({ "standard" : "ISO", "engagement" : "75%", "pitch" : "0.8 mm", "size" : "M5", "type" : "Tapped" }), "holeDiameter" : 4.2 * mm, "majorDiameter" : 5 * mm, "showTappedDepth" : true, "isTappedThrough" : true, "tappedDepth" : 10.4 * mm, "tapClearance" : 3, "locations" : qUnion([Q0, Q1, Q2, Q3, Q4, Q5, Q6, Q7, Q8, Q9, Q10, Q11, Q12, Q13, Q14, Q15, Q16, Q17]), "scope" : qUnion([Q18])});
        }
        {
            var Q0;
            Q0=sQuery(id+"F27.wireOp",VERTEX,"E90.center");
            var Q1;
            Q1=sQuery(id+"F27.wireOp",VERTEX,"E89.center");
            var Q2;
            Q2=sQuery(id+"F27.wireOp",VERTEX,"E91.center");
            var Q3;
            Q3=sQuery(id+"F27.wireOp",VERTEX,"E88.center");
            var Q4;
            Q4=makeQuery(id+"F18.opExtrude","SWEPT_BODY",BODY,{"disambiguationData":[OSD([sQuery(id+"F17.wireOp",EDGE,"E29.0"),sQuery(id+"F17.wireOp",EDGE,"E29.1"),sQuery(id+"F17.wireOp",EDGE,"E29.2"),sQuery(id+"F17.wireOp",EDGE,"E29.3"),sQuery(id+"F17.wireOp",EDGE,"E29.4"),sQuery(id+"F17.wireOp",EDGE,"E29.5"),sQuery(id+"F17.wireOp",EDGE,"E29.6"),sQuery(id+"F17.wireOp",EDGE,"E29.7")])]});
            hole(context, id + "F32", {"style" : HoleStyle.SIMPLE, "endStyle" : HoleEndStyle.THROUGH, "standardTappedOrClearance" : lookupTablePath({ "standard" : "ISO", "engagement" : "75%", "pitch" : "0.8 mm", "size" : "M5", "type" : "Tapped" }), "standardBlindInLast" : lookupTablePath({ "standard" : "ISO", "engagement" : "75%", "pitch" : "0.8 mm", "size" : "M5", "type" : "Tapped" }), "holeDiameter" : 4.2 * mm, "majorDiameter" : 5 * mm, "showTappedDepth" : true, "isTappedThrough" : true, "tappedDepth" : 10.4 * mm, "tapClearance" : 3, "locations" : qUnion([Q0, Q1, Q2, Q3]), "scope" : qUnion([Q4])});
        }
        {
            var Q0;
            Q0=sQuery(id+"F22.wireOp",VERTEX,"E51.0.0.center");
            var Q1;
            Q1=sQuery(id+"F22.wireOp",VERTEX,"E52.0.0.center");
            var Q2;
            Q2=sQuery(id+"F22.wireOp",VERTEX,"E53.0.0.center");
            var Q3;
            Q3=sQuery(id+"F22.wireOp",VERTEX,"E54.0.0.center");
            var Q4;
            Q4=makeQuery(id+"F18.opExtrude","SWEPT_BODY",BODY,{"disambiguationData":[OSD([sQuery(id+"F17.wireOp",EDGE,"E29.0"),sQuery(id+"F17.wireOp",EDGE,"E29.1"),sQuery(id+"F17.wireOp",EDGE,"E29.2"),sQuery(id+"F17.wireOp",EDGE,"E29.3"),sQuery(id+"F17.wireOp",EDGE,"E29.4"),sQuery(id+"F17.wireOp",EDGE,"E29.5"),sQuery(id+"F17.wireOp",EDGE,"E29.6"),sQuery(id+"F17.wireOp",EDGE,"E29.7")])]});
            hole(context, id + "F33", {"style" : HoleStyle.SIMPLE, "endStyle" : HoleEndStyle.THROUGH, "standardTappedOrClearance" : lookupTablePath({ "standard" : "ISO", "engagement" : "75%", "pitch" : "1 mm", "size" : "M6", "type" : "Tapped" }), "standardBlindInLast" : lookupTablePath({ "standard" : "ISO", "engagement" : "75%", "pitch" : "1 mm", "size" : "M6", "type" : "Tapped" }), "holeDiameter" : 5 * mm, "majorDiameter" : 6 * mm, "showTappedDepth" : true, "isTappedThrough" : true, "tappedDepth" : 10.4 * mm, "tapClearance" : 3, "locations" : qUnion([Q0, Q1, Q2, Q3]), "scope" : qUnion([Q4])});
        }
        {
            var Q0;
            {var subQ0=sQuery(id+"F0.wireOp",EDGE,"E0.top");Q0=makeQuery(id+"F4.opShell","OFFSET_FACE",FACE,{"disambiguationData":[OSD([subQ0]),TDD([makeQuery(id+"F1.opExtrude","SWEPT_FACE",FACE,{"disambiguationData":[OSD([subQ0])]})])]});}
            var sketch = newSketch(context, id + "F34", { "sketchPlane" : qUnion([Q0])});
            skLineSegment(sketch, "E104.bottom", {"start": v(313.01, 128.19) * mm, "end": v(-303.12, 128.19) * mm});
            skLineSegment(sketch, "E104.top", {"start": v(313.01, 588.78) * mm, "end": v(-303.12, 588.78) * mm});
            skLineSegment(sketch, "E104.left", {"start": v(313.01, 128.19) * mm, "end": v(313.01, 588.78) * mm});
            skLineSegment(sketch, "E104.right", {"start": v(-303.12, 128.19) * mm, "end": v(-303.12, 588.78) * mm});
            skLineSegment(sketch, "E105.bottom", {"start": v(-306.57, 592.92) * mm, "end": v(315.84, 592.92) * mm});
            skLineSegment(sketch, "E105.top", {"start": v(-306.57, 124.24) * mm, "end": v(315.84, 124.24) * mm});
            skLineSegment(sketch, "E105.left", {"start": v(-306.57, 592.92) * mm, "end": v(-306.57, 124.24) * mm});
            skLineSegment(sketch, "E105.right", {"start": v(315.84, 592.92) * mm, "end": v(315.84, 124.24) * mm});
            skSolve(sketch);
        }
        {
            var Q0;
            Q0 = qSketchRegion(id + "F34", true);
            extrude(context, id + "F35", {"entities" : qUnion([Q0]), "operationType" : NewBodyOperationType.ADD, "depth" : 25 * mm, "offsetDistance" : 25 * mm});
        }
        {
            var Q0;
            Q0=makeQuery(id+"F35.opExtrude","CAP_FACE",FACE,{"disambiguationData":[OSD([sQuery(id+"F34.wireOp",EDGE,"E104.bottom"),sQuery(id+"F34.wireOp",EDGE,"E104.top"),sQuery(id+"F34.wireOp",EDGE,"E104.left"),sQuery(id+"F34.wireOp",EDGE,"E104.right"),sQuery(id+"F34.wireOp",EDGE,"E105.bottom"),sQuery(id+"F34.wireOp",EDGE,"E105.top"),sQuery(id+"F34.wireOp",EDGE,"E105.left"),sQuery(id+"F34.wireOp",EDGE,"E105.right")])],"isStart":false});
            var sketch = newSketch(context, id + "F36", { "sketchPlane" : qUnion([Q0])});
            skLineSegment(sketch, "E106.bottom", {"start": v(315.84, 124.24) * mm, "end": v(-306.57, 124.24) * mm});
            skLineSegment(sketch, "E106.top", {"start": v(315.84, 592.92) * mm, "end": v(-306.57, 592.92) * mm});
            skLineSegment(sketch, "E106.left", {"start": v(315.84, 124.24) * mm, "end": v(315.84, 592.92) * mm});
            skLineSegment(sketch, "E106.right", {"start": v(-306.57, 124.24) * mm, "end": v(-306.57, 592.92) * mm});
            skArc(sketch, "E107.0", {"start": v(-300, 575) * mm, "mid": v(-297.07, 582.07) * mm, "end": v(-290, 585) * mm});
            skLineSegment(sketch, "E108.0", {"start": v(-290, 585) * mm, "end": v(290, 585) * mm});
            skLineSegment(sketch, "E109.0", {"start": v(-300, 145) * mm, "end": v(-300, 575) * mm});
            skArc(sketch, "E110.0", {"start": v(-290, 135) * mm, "mid": v(-297.07, 137.93) * mm, "end": v(-300, 145) * mm});
            skLineSegment(sketch, "E111.0", {"start": v(-290, 135) * mm, "end": v(290, 135) * mm});
            skArc(sketch, "E112.0", {"start": v(300, 145) * mm, "mid": v(297.07, 137.93) * mm, "end": v(290, 135) * mm});
            skLineSegment(sketch, "E113.0", {"start": v(300, 145) * mm, "end": v(300, 575) * mm});
            skArc(sketch, "E114.0", {"start": v(290, 585) * mm, "mid": v(297.07, 582.07) * mm, "end": v(300, 575) * mm});
            skLineSegment(sketch, "E115.0", {"start": v(275, 170) * mm, "end": v(275, 550) * mm});
            skLineSegment(sketch, "E115.1", {"start": v(-265, 160) * mm, "end": v(265, 160) * mm});
            skLineSegment(sketch, "E115.2", {"start": v(-275, 170) * mm, "end": v(-275, 550) * mm});
            skLineSegment(sketch, "E115.3", {"start": v(-265, 560) * mm, "end": v(265, 560) * mm});
            skPoint(sketch, "E116.visualSharp", {"position": v(275, 560) * mm});
            skArc(sketch, "E116.filletArc", {"start": v(275, 550) * mm, "mid": v(272.07, 557.07) * mm, "end": v(265, 560) * mm});
            skPoint(sketch, "E117.visualSharp", {"position": v(275, 160) * mm});
            skArc(sketch, "E117.filletArc", {"start": v(265, 160) * mm, "mid": v(272.07, 162.93) * mm, "end": v(275, 170) * mm});
            skPoint(sketch, "E118.visualSharp", {"position": v(-275, 560) * mm});
            skArc(sketch, "E118.filletArc", {"start": v(-265, 560) * mm, "mid": v(-272.07, 557.07) * mm, "end": v(-275, 550) * mm});
            skPoint(sketch, "E119.visualSharp", {"position": v(-275, 160) * mm});
            skArc(sketch, "E119.filletArc", {"start": v(-275, 170) * mm, "mid": v(-272.07, 162.93) * mm, "end": v(-265, 160) * mm});
            skSolve(sketch);
        }
        {
            var Q0;
            Q0=makeQuery(id+"F36.imprint","IMPRINT",FACE,{"disambiguationData":[TD([[makeQuery(id+"F36.imprint","IMPRINT",EDGE,{"derivedFrom":sQuery(id+"F36.wireOp",EDGE,"E106.bottom")}),1.0]])]});
            var Q1;
            Q1=makeQuery(id+"F36.imprint","IMPRINT",FACE,{"disambiguationData":[TD([[makeQuery(id+"F36.imprint","IMPRINT",EDGE,{"derivedFrom":sQuery(id+"F36.wireOp",EDGE,"E107.0")}),-1.0]])]});
            var Q2;
            Q2=makeQuery(id+"F36.imprint","IMPRINT",FACE,{"disambiguationData":[TD([[makeQuery(id+"F36.imprint","IMPRINT",EDGE,{"derivedFrom":sQuery(id+"F36.wireOp",EDGE,"E107.0")}),1.0]])]});
            extrude(context, id + "F37", {"entities" : qUnion([Q0, Q1, Q2]), "operationType" : NewBodyOperationType.ADD, "depth" : 3 * mm, "offsetDistance" : 25 * mm});
        }
    });
